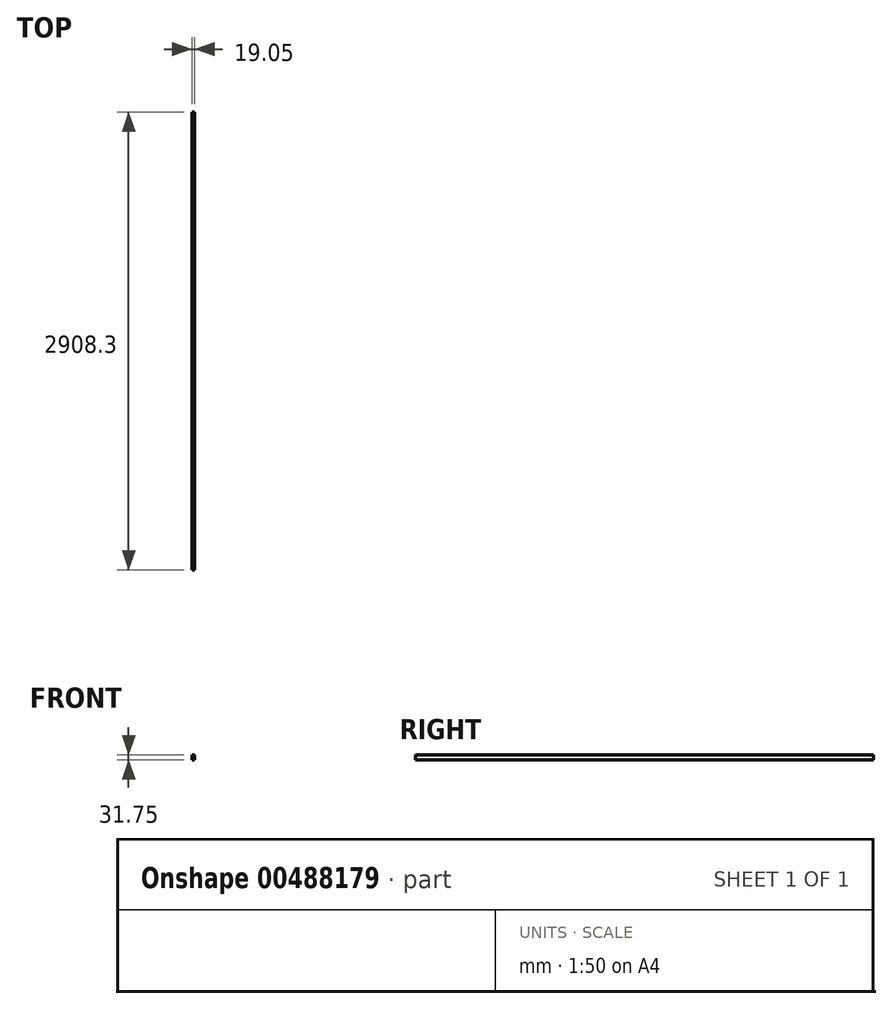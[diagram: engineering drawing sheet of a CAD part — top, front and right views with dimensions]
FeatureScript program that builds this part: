
annotation { "Feature Type Name" : "Feature", "Feature Type Description" : "" }
export const myFeature = defineFeature(function(context is Context, id is Id, definition is map)
    precondition{}
    {
        {
            var Q0;
            Q0=qCreatedBy(makeId("Front.planeOp"),FACE);
            var sketch = newSketch(context, id + "F0", { "sketchPlane" : qUnion([Q0])});
            skLineSegment(sketch, "E0", {"start": v(0, 0) * mm, "end": v(0, 31.75) * mm});
            skLineSegment(sketch, "E1", {"start": v(0, 31.75) * mm, "end": v(19.05, 31.75) * mm});
            skLineSegment(sketch, "E2", {"start": v(19.05, 31.75) * mm, "end": v(19.05, 0) * mm});
            skLineSegment(sketch, "E3", {"start": v(19.05, 0) * mm, "end": v(0, 0) * mm});
            skSolve(sketch);
        }
        {
            var Q0;
            Q0=makeQuery(id+"F0.imprint","IMPRINT",FACE,{"disambiguationData":[TD([[makeQuery(id+"F0.imprint","IMPRINT",EDGE,{"derivedFrom":sQuery(id+"F0.wireOp",EDGE,"E0")}),-1.0]])]});
            extrude(context, id + "F1", {"entities" : qUnion([Q0]), "depth" : 2743.2 * mm + 165.1 * mm, "offsetDistance" : 25.4 * mm});
        }
    });
